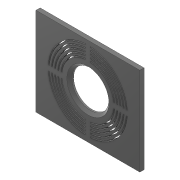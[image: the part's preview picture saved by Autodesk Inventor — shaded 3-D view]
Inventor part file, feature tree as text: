
AUTODESK INVENTOR PART (.ipt)
format: ipt  version: 2020 (Build 240168000, 168)  size: 284,672 bytes
history: native  units: mm
features: extrude x5, sketch x5, chamfer x2
ambient origin geometry x8: Origin, YZ Plane, XZ Plane, XY Plane, X Axis, Y Axis, Z Axis, Center Point
bodies: Volumenkörper1 (feature_tree)
feature tree (12):
  extrude  "Extrusion1"  Depth=85.0mm
  extrude  "Extrusion2"  Depth=4.0mm
  chamfer  "Fase1"  Distance=1000.0mm
  extrude  "Extrusion3"  Depth=50.0mm
  extrude  "Extrusion4"  Depth=10.0mm
  chamfer  "Fase2"  Distance=58.0mm
  extrude  "Extrusion5"  Depth=10.0mm
  sketch  "Skizze1"  dims[d0=100.0mm d1=85.0mm]
  sketch  "Skizze2"  dims[d2=4.0mm d3=0.0mm d4=50.0mm]
  sketch  "Skizze3"  dims[d5=43.0mm d6=1000.0mm d7=0.0mm]
  sketch  "Skizze4"  dims[d8=2.5mm d9=2.0mm d10=45.0deg d11=50.0mm]
  sketch  "Skizze5"  dims[d12=52.0mm d13=56.0mm d14=58.0mm d15=62.0mm d16=64.0mm d17=68.0mm d18=70.0mm d19=1000.0mm d20=0.0mm d21=74.0mm d22=76.0mm d23=40.0mm d24=5.0mm d25=2.5mm d26=0.0mm d27=40.0mm d28=38.5mm d29=5.0mm d30=2.5mm d31=40.0mm d32=5.0mm d33=4.0mm d34=0.0mm d35=2.5mm d36=2.0mm d37=45.0deg d38=0.1mm d39=0.1mm d40=0.1mm d41=0.1mm d42=10.0mm d43=0.0mm]
